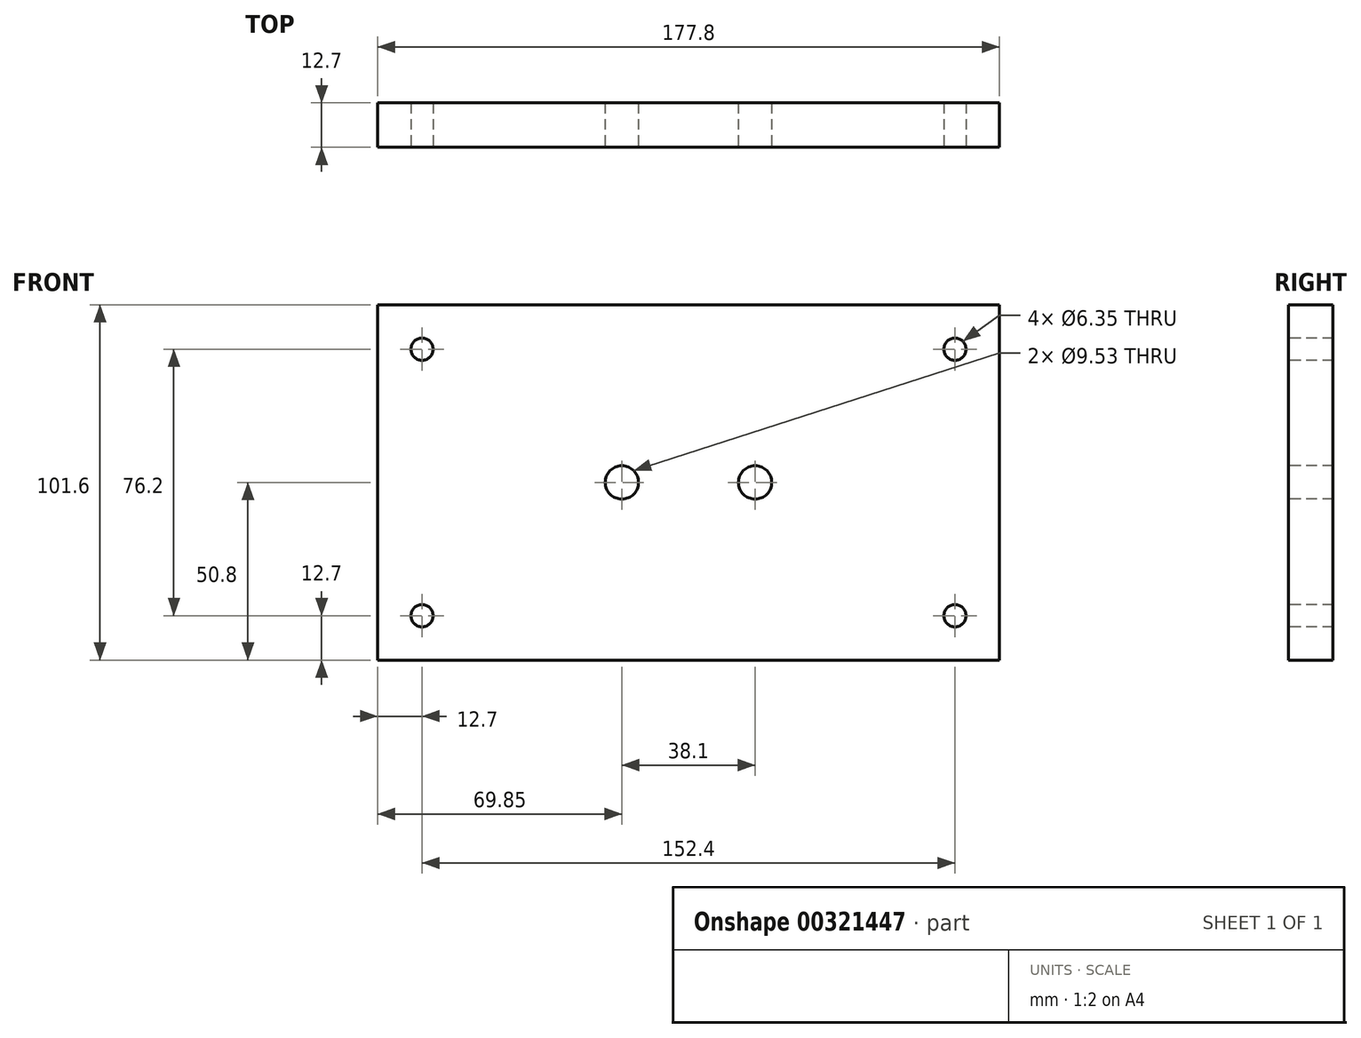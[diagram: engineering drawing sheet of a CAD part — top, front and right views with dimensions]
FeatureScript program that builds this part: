
annotation { "Feature Type Name" : "Feature", "Feature Type Description" : "" }
export const myFeature = defineFeature(function(context is Context, id is Id, definition is map)
    precondition{}
    {
        {
            var Q0;
            Q0=qCreatedBy(makeId("Front.planeOp"),FACE);
            var sketch = newSketch(context, id + "F0", { "sketchPlane" : qUnion([Q0])});
            skLineSegment(sketch, "E0.bottom", {"start": v(88.9, -50.8) * mm, "end": v(-88.9, -50.8) * mm});
            skLineSegment(sketch, "E0.top", {"start": v(88.9, 50.8) * mm, "end": v(-88.9, 50.8) * mm});
            skLineSegment(sketch, "E0.left", {"start": v(88.9, -50.8) * mm, "end": v(88.9, 50.8) * mm});
            skLineSegment(sketch, "E0.right", {"start": v(-88.9, -50.8) * mm, "end": v(-88.9, 50.8) * mm});
            skPoint(sketch, "E0.middle", {"position": v(0, 0) * mm});
            skSolve(sketch);
        }
        {
            var Q0;
            Q0 = qSketchRegion(id + "F0", true);
            extrude(context, id + "F1", {"entities" : qUnion([Q0]), "depth" : 12.7 * mm});
        }
        {
            var Q0;
            Q0=makeQuery(id+"F1.opExtrude","CAP_FACE",FACE,{"disambiguationData":[OSD([sQuery(id+"F0.wireOp",EDGE,"E0.bottom"),sQuery(id+"F0.wireOp",EDGE,"E0.top"),sQuery(id+"F0.wireOp",EDGE,"E0.left"),sQuery(id+"F0.wireOp",EDGE,"E0.right")])],"isStart":false});
            var sketch = newSketch(context, id + "F2", { "sketchPlane" : qUnion([Q0])});
            skCircle(sketch, "E1", {"center": v(-76.2, 38.1) * mm, "radius": 3.18 * mm});
            skCircle(sketch, "E2.MirrorC", {"center": v(76.2, 38.1) * mm, "radius": 3.18 * mm});
            skCircle(sketch, "E3.MirrorC", {"center": v(-76.2, -38.1) * mm, "radius": 3.18 * mm});
            skCircle(sketch, "E4.MirrorC", {"center": v(76.2, -38.1) * mm, "radius": 3.18 * mm});
            skLineSegment(sketch, "E5", {"start": v(-19.05, 0) * mm, "end": v(19.05, 0) * mm, "construction": true});
            skPoint(sketch, "E6", {"position": v(0, 0) * mm});
            skCircle(sketch, "E7", {"center": v(-19.05, 0) * mm, "radius": 4.76 * mm});
            skCircle(sketch, "E8", {"center": v(19.05, 0) * mm, "radius": 4.76 * mm});
            skSolve(sketch);
        }
        {
            var Q0;
            Q0 = qSketchRegion(id + "F2", true);
            extrude(context, id + "F3", {"entities" : qUnion([Q0]), "operationType" : NewBodyOperationType.REMOVE, "endBound" : BoundingType.THROUGH_ALL, "oppositeDirection" : true, "depth" : 25.4 * mm});
        }
    });
